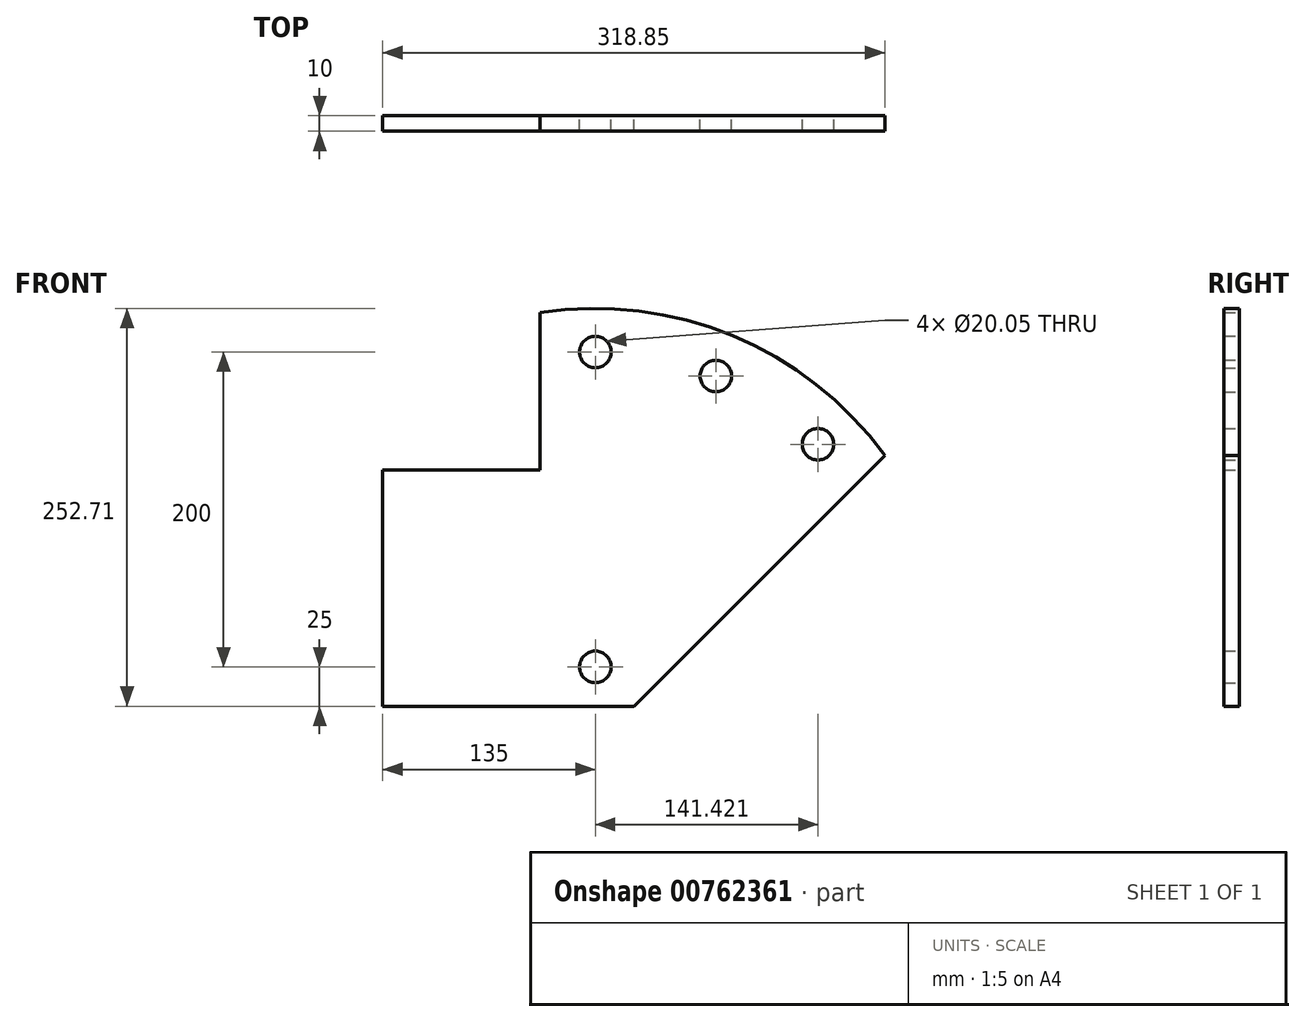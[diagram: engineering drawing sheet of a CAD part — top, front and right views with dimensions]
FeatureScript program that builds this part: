
annotation { "Feature Type Name" : "Feature", "Feature Type Description" : "" }
export const myFeature = defineFeature(function(context is Context, id is Id, definition is map)
    precondition{}
    {
        {
            var Q0;
            Q0=qCreatedBy(makeId("Front.planeOp"),FACE);
            var sketch = newSketch(context, id + "F0", { "sketchPlane" : qUnion([Q0])});
            skLineSegment(sketch, "E0", {"start": v(0, 0) * mm, "end": v(-100, 0) * mm});
            skLineSegment(sketch, "E1", {"start": v(-100, 0) * mm, "end": v(-100, -150) * mm});
            skLineSegment(sketch, "E2", {"start": v(-100, -150) * mm, "end": v(59.5, -150) * mm});
            skLineSegment(sketch, "E3", {"start": v(59.5, -150) * mm, "end": v(218.85, 9.35) * mm});
            skLineSegment(sketch, "E4", {"start": v(0, 0) * mm, "end": v(0, 100) * mm});
            skArc(sketch, "E5", {"start": v(218.85, 9.35) * mm, "mid": v(122.14, 85.37) * mm, "end": v(0, 100) * mm});
            skCircle(sketch, "E6", {"center": v(35, 75) * mm, "radius": 10.03 * mm});
            skCircle(sketch, "E7", {"center": v(111.54, 59.78) * mm, "radius": 10.03 * mm});
            skCircle(sketch, "E8", {"center": v(176.42, 16.42) * mm, "radius": 10.03 * mm});
            skCircle(sketch, "E9", {"center": v(35, -125) * mm, "radius": 10.03 * mm});
            skLineSegment(sketch, "E10", {"start": v(35, 75) * mm, "end": v(35, -125) * mm, "construction": true});
            skLineSegment(sketch, "E11", {"start": v(35, -125) * mm, "end": v(176.42, 16.42) * mm, "construction": true});
            skLineSegment(sketch, "E12", {"start": v(111.54, 59.78) * mm, "end": v(35, -125) * mm, "construction": true});
            skArc(sketch, "E13", {"start": v(176.42, 16.42) * mm, "mid": v(111.54, 59.78) * mm, "end": v(35, 75) * mm, "construction": true});
            skSolve(sketch);
        }
        {
            var Q0;
            Q0 = qSketchRegion(id + "F0", true);
            extrude(context, id + "F1", {"entities" : qUnion([Q0]), "depth" : 10 * mm, "offsetDistance" : 25 * mm});
        }
    });
